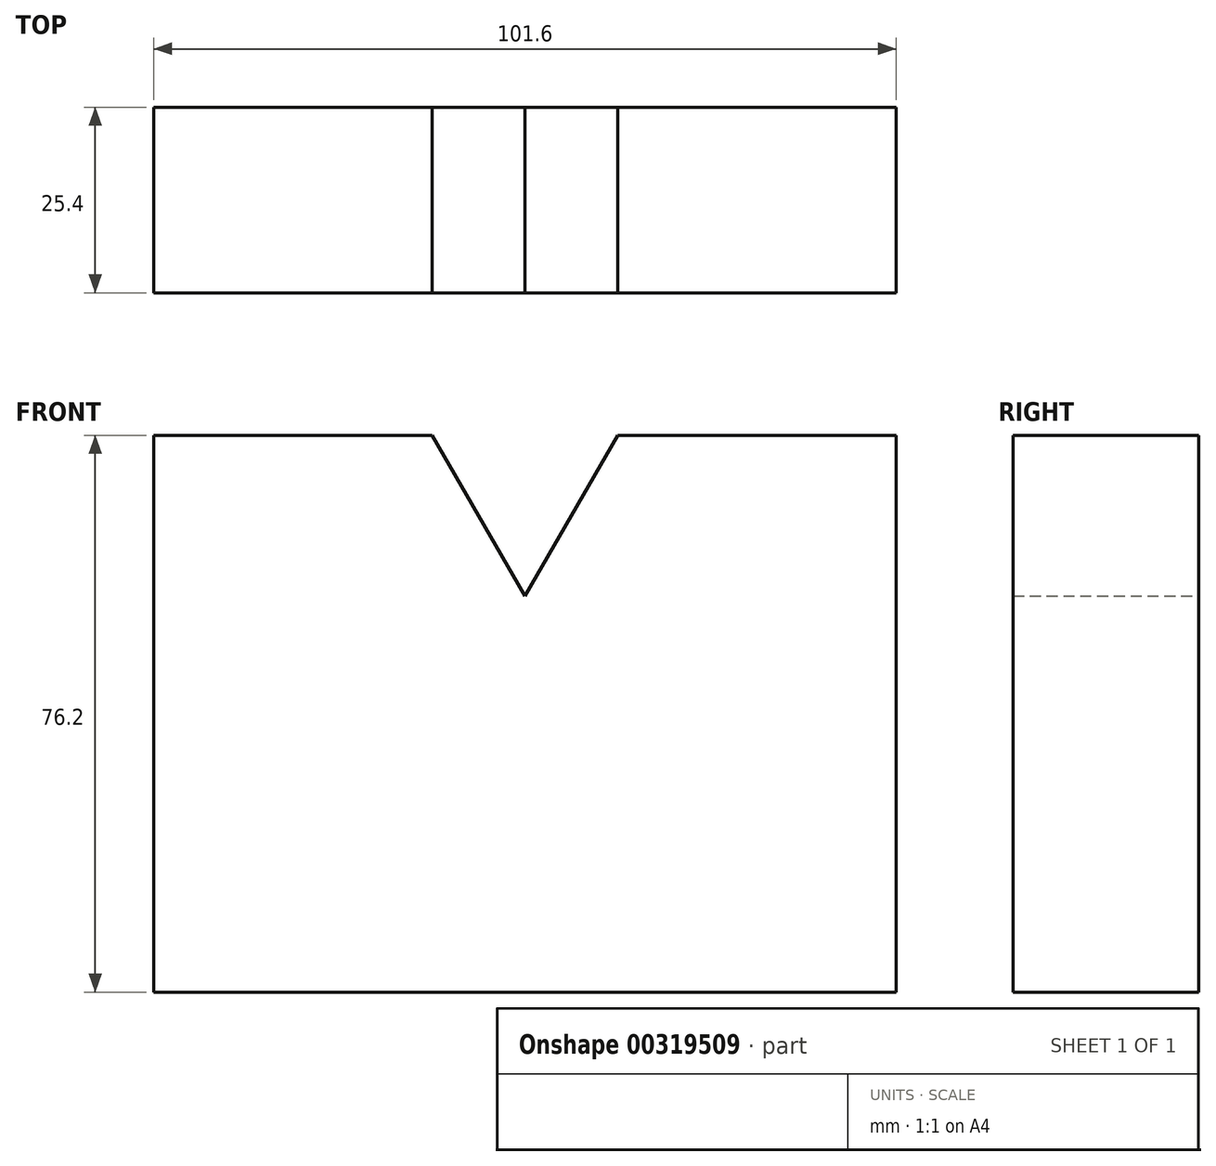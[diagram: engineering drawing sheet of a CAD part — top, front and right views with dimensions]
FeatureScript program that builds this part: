
annotation { "Feature Type Name" : "Feature", "Feature Type Description" : "" }
export const myFeature = defineFeature(function(context is Context, id is Id, definition is map)
    precondition{}
    {
        {
            var Q0;
            Q0=qCreatedBy(makeId("Front.planeOp"),FACE);
            var sketch = newSketch(context, id + "F0", { "sketchPlane" : qUnion([Q0])});
            skLineSegment(sketch, "E0", {"start": v(-51.42, -46.27) * mm, "end": v(50.18, -46.27) * mm});
            skLineSegment(sketch, "E1", {"start": v(50.18, -46.27) * mm, "end": v(50.18, 29.93) * mm});
            skLineSegment(sketch, "E2", {"start": v(-51.42, -46.27) * mm, "end": v(-51.42, 29.93) * mm});
            skLineSegment(sketch, "E3", {"start": v(-51.42, 29.93) * mm, "end": v(-13.32, 29.93) * mm});
            skLineSegment(sketch, "E4", {"start": v(50.18, 29.93) * mm, "end": v(12.08, 29.93) * mm});
            skLineSegment(sketch, "E5", {"start": v(12.08, 29.93) * mm, "end": v(-0.62, 7.93) * mm});
            skLineSegment(sketch, "E6", {"start": v(-13.32, 29.93) * mm, "end": v(-0.62, 7.93) * mm});
            skSolve(sketch);
        }
        {
            var Q0;
            Q0=makeQuery(id+"F0.imprint","IMPRINT",FACE,{"disambiguationData":[TD([[makeQuery(id+"F0.imprint","IMPRINT",EDGE,{"derivedFrom":sQuery(id+"F0.wireOp",EDGE,"E0")}),1.0]])]});
            extrude(context, id + "F1", {"entities" : qUnion([Q0]), "depth" : 25.4 * mm});
        }
    });
